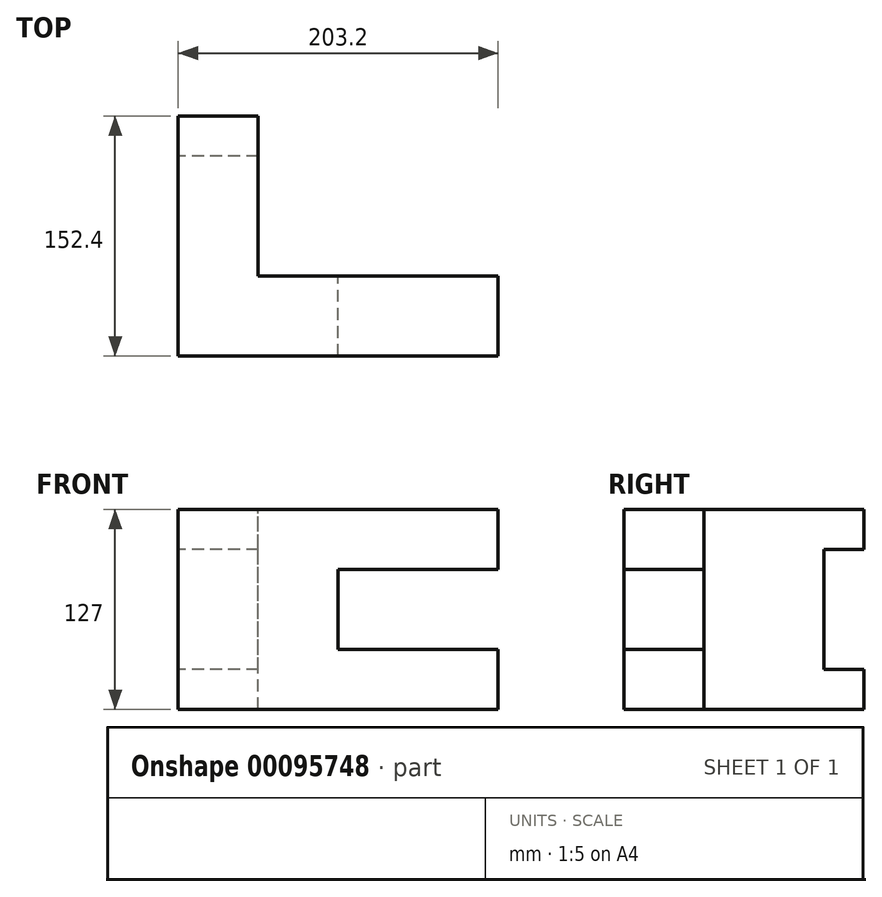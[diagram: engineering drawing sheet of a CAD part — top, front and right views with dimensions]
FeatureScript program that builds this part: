
annotation { "Feature Type Name" : "Feature", "Feature Type Description" : "" }
export const myFeature = defineFeature(function(context is Context, id is Id, definition is map)
    precondition{}
    {
        {
            var Q0;
            Q0=qCreatedBy(makeId("Front.planeOp"),FACE);
            var sketch = newSketch(context, id + "F0", { "sketchPlane" : qUnion([Q0])});
            skLineSegment(sketch, "E0", {"start": v(-103.17, 58.86) * mm, "end": v(100.03, 58.86) * mm});
            skLineSegment(sketch, "E1", {"start": v(100.03, 58.86) * mm, "end": v(100.03, 20.76) * mm});
            skLineSegment(sketch, "E2", {"start": v(100.03, 20.76) * mm, "end": v(-1.57, 20.76) * mm});
            skLineSegment(sketch, "E3", {"start": v(-1.57, 20.76) * mm, "end": v(-1.57, -30.04) * mm});
            skLineSegment(sketch, "E4", {"start": v(-1.57, -30.04) * mm, "end": v(100.03, -30.04) * mm});
            skLineSegment(sketch, "E5", {"start": v(100.03, -30.04) * mm, "end": v(100.03, -68.14) * mm});
            skLineSegment(sketch, "E6", {"start": v(100.03, -68.14) * mm, "end": v(-103.17, -68.14) * mm});
            skLineSegment(sketch, "E7", {"start": v(-103.17, 58.86) * mm, "end": v(-103.17, -68.14) * mm});
            skSolve(sketch);
        }
        {
            var Q0;
            Q0=makeQuery(id+"F0.imprint","IMPRINT",FACE,{"disambiguationData":[TD([[makeQuery(id+"F0.imprint","IMPRINT",EDGE,{"derivedFrom":sQuery(id+"F0.wireOp",EDGE,"E0")}),-1.0]])]});
            extrude(context, id + "F1", {"entities" : qUnion([Q0]), "depth" : 50.8 * mm});
        }
        {
            var Q0;
            Q0=makeQuery(id+"F1.opExtrude","CAP_FACE",FACE,{"disambiguationData":[OSD([sQuery(id+"F0.wireOp",EDGE,"E0"),sQuery(id+"F0.wireOp",EDGE,"E1"),sQuery(id+"F0.wireOp",EDGE,"E2"),sQuery(id+"F0.wireOp",EDGE,"E3"),sQuery(id+"F0.wireOp",EDGE,"E4"),sQuery(id+"F0.wireOp",EDGE,"E5"),sQuery(id+"F0.wireOp",EDGE,"E6"),sQuery(id+"F0.wireOp",EDGE,"E7")])],"isStart":true});
            var sketch = newSketch(context, id + "F2", { "sketchPlane" : qUnion([Q0])});
            skLineSegment(sketch, "E8.bottom", {"start": v(103.17, -68.14) * mm, "end": v(52.37, -68.14) * mm});
            skLineSegment(sketch, "E8.top", {"start": v(103.17, 58.86) * mm, "end": v(52.37, 58.86) * mm});
            skLineSegment(sketch, "E8.left", {"start": v(103.17, -68.14) * mm, "end": v(103.17, 58.86) * mm});
            skLineSegment(sketch, "E8.right", {"start": v(52.37, -68.14) * mm, "end": v(52.37, 58.86) * mm});
            skSolve(sketch);
        }
        {
            var Q0;
            Q0 = qSketchRegion(id + "F2", true);
            extrude(context, id + "F3", {"entities" : qUnion([Q0]), "operationType" : NewBodyOperationType.ADD, "depth" : 76.2 * mm});
        }
        {
            var Q0;
            Q0=makeQuery(id+"F3.opExtrude","CAP_FACE",FACE,{"disambiguationData":[OSD([sQuery(id+"F2.wireOp",EDGE,"E8.bottom"),sQuery(id+"F2.wireOp",EDGE,"E8.top"),sQuery(id+"F2.wireOp",EDGE,"E8.left"),sQuery(id+"F2.wireOp",EDGE,"E8.right")])],"isStart":false});
            var sketch = newSketch(context, id + "F4", { "sketchPlane" : qUnion([Q0])});
            skLineSegment(sketch, "E9.bottom", {"start": v(52.37, 58.86) * mm, "end": v(103.17, 58.86) * mm});
            skLineSegment(sketch, "E9.top", {"start": v(52.37, 33.46) * mm, "end": v(103.17, 33.46) * mm});
            skLineSegment(sketch, "E9.left", {"start": v(52.37, 58.86) * mm, "end": v(52.37, 33.46) * mm});
            skLineSegment(sketch, "E9.right", {"start": v(103.17, 58.86) * mm, "end": v(103.17, 33.46) * mm});
            skLineSegment(sketch, "E10.bottom", {"start": v(52.37, -68.14) * mm, "end": v(103.17, -68.14) * mm});
            skLineSegment(sketch, "E10.top", {"start": v(52.37, -42.74) * mm, "end": v(103.17, -42.74) * mm});
            skLineSegment(sketch, "E10.left", {"start": v(52.37, -68.14) * mm, "end": v(52.37, -42.74) * mm});
            skLineSegment(sketch, "E10.right", {"start": v(103.17, -68.14) * mm, "end": v(103.17, -42.74) * mm});
            skSolve(sketch);
        }
        {
            var Q0;
            Q0 = qSketchRegion(id + "F4", true);
            extrude(context, id + "F5", {"entities" : qUnion([Q0]), "operationType" : NewBodyOperationType.ADD, "depth" : 25.4 * mm});
        }
    });
